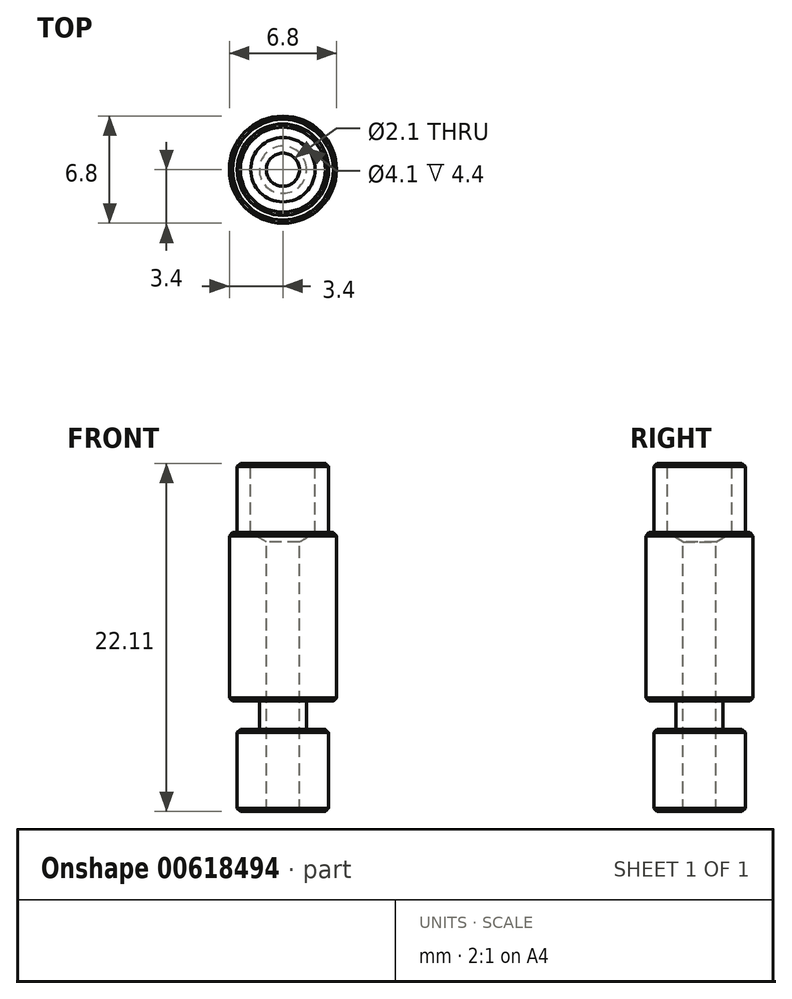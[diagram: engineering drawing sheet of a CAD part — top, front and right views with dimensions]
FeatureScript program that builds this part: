
annotation { "Feature Type Name" : "Feature", "Feature Type Description" : "" }
export const myFeature = defineFeature(function(context is Context, id is Id, definition is map)
    precondition{}
    {
        {
            var Q0;
            Q0=qCreatedBy(makeId("Top.planeOp"),FACE);
            var sketch = newSketch(context, id + "F0", { "sketchPlane" : qUnion([Q0])});
            skCircle(sketch, "E0", {"center": v(0, 0) * mm, "radius": 1.5 * mm});
            skCircle(sketch, "E1", {"center": v(0, 0) * mm, "radius": 2.9 * mm});
            skCircle(sketch, "E2", {"center": v(0, 0) * mm, "radius": 3.4 * mm});
            skSolve(sketch);
        }
        {
            var Q0;
            Q0=makeQuery(id+"F0.imprint","IMPRINT",FACE,{"disambiguationData":[TD([[makeQuery(id+"F0.imprint","IMPRINT",EDGE,{"derivedFrom":sQuery(id+"F0.wireOp",EDGE,"E0")}),-1.0]])]});
            var Q1;
            Q1=makeQuery(id+"F0.imprint","IMPRINT",FACE,{"disambiguationData":[TD([[makeQuery(id+"F0.imprint","IMPRINT",EDGE,{"derivedFrom":sQuery(id+"F0.wireOp",EDGE,"E0")}),1.0]])]});
            extrude(context, id + "F1", {"entities" : qUnion([Q0, Q1]), "depth" : 22.1 * mm, "offsetDistance" : 25 * mm});
        }
        {
            var Q0;
            Q0=makeQuery(id+"F0.imprint","IMPRINT",FACE,{"disambiguationData":[TD([[makeQuery(id+"F0.imprint","IMPRINT",EDGE,{"derivedFrom":sQuery(id+"F0.wireOp",EDGE,"E1")}),-1.0]])]});
            extrude(context, id + "F2", {"entities" : qUnion([Q0]), "operationType" : NewBodyOperationType.ADD, "depth" : 17.7 * mm, "offsetDistance" : 25 * mm, "hasSecondDirection" : true, "secondDirectionOppositeDirection" : false, "secondDirectionDepth" : 7 * mm});
        }
        {
            var Q0;
            Q0=makeQuery(id+"F0.imprint","IMPRINT",FACE,{"disambiguationData":[TD([[makeQuery(id+"F0.imprint","IMPRINT",EDGE,{"derivedFrom":sQuery(id+"F0.wireOp",EDGE,"E1")}),-1.0]])]});
            var Q1;
            Q1=makeQuery(id+"F0.imprint","IMPRINT",FACE,{"disambiguationData":[TD([[makeQuery(id+"F0.imprint","IMPRINT",EDGE,{"derivedFrom":sQuery(id+"F0.wireOp",EDGE,"E0")}),-1.0]])]});
            var Q2;
            Q2=makeQuery(id+"F2.opExtrude","CAP_FACE",FACE,{"disambiguationData":[OSD([sQuery(id+"F0.wireOp",EDGE,"E1"),sQuery(id+"F0.wireOp",EDGE,"E2")])],"isStart":true});
            extrude(context, id + "F3", {"entities" : qUnion([Q0, Q1]), "operationType" : NewBodyOperationType.REMOVE, "endBound" : BoundingType.UP_TO_SURFACE, "depth" : 12 * mm, "endBoundEntityFace" : qUnion([Q2]), "offsetDistance" : 25 * mm, "hasSecondDirection" : true, "secondDirectionOppositeDirection" : false, "secondDirectionDepth" : 5.2 * mm});
        }
        {
            var Q0;
            Q0=makeQuery(id+"F1.opExtrude","CAP_FACE",FACE,{"disambiguationData":[OSD([sQuery(id+"F0.wireOp",EDGE,"E1")])],"isStart":false});
            var sketch = newSketch(context, id + "F4", { "sketchPlane" : qUnion([Q0])});
            skPoint(sketch, "E3", {"position": v(0, 0) * mm});
            skSolve(sketch);
        }
        {
            var Q0;
            Q0=sQuery(id+"F4.wireOp",VERTEX,"E3");
            var Q1;
            Q1=makeQuery(id+"F1.opExtrude","SWEPT_BODY",BODY,{"disambiguationData":[OSD([sQuery(id+"F0.wireOp",EDGE,"E1")])]});
            hole(context, id + "F5", {"style" : HoleStyle.SIMPLE, "endStyle" : HoleEndStyle.THROUGH, "holeDiameter" : 2.1 * mm, "majorDiameter" : 5 * mm, "isTappedThrough" : true, "tappedDepth" : 12 * mm, "tapClearance" : 3, "locations" : qUnion([Q0]), "scope" : qUnion([Q1])});
        }
        {
            var Q0;
            Q0=sQuery(id+"F4.wireOp",VERTEX,"E3");
            var Q1;
            Q1=makeQuery(id+"F1.opExtrude","SWEPT_BODY",BODY,{"disambiguationData":[OSD([sQuery(id+"F0.wireOp",EDGE,"E1")])]});
            hole(context, id + "F6", {"style" : HoleStyle.SIMPLE, "endStyle" : HoleEndStyle.BLIND, "holeDiameter" : 4.1 * mm, "majorDiameter" : 5 * mm, "holeDepth" : 4.4 * mm, "isTappedThrough" : true, "tappedDepth" : 12 * mm, "tapClearance" : 3, "locations" : qUnion([Q0]), "scope" : qUnion([Q1])});
        }
        {
            var Q0;
            Q0=makeQuery(id+"F1.opExtrude","CAP_EDGE",EDGE,{"disambiguationData":[OSD([sQuery(id+"F0.wireOp",EDGE,"E1")])],"isStart":false});
            var Q1;
            {var subQ0=sQuery(id+"F0.wireOp",EDGE,"E2");var subQ1=sQuery(id+"F0.wireOp",EDGE,"E1");Q1=makeQuery(id+"F3.boolean.opBoolean","INTERSECT",EDGE,{"derivedFrom":[makeQuery(id+"F2.boolean.opBoolean","SPLIT",FACE,{"disambiguationData":[TD([makeQuery(id+"F1.opExtrude","CAP_FACE",FACE,{"disambiguationData":[OSD([subQ1])],"isStart":true})])],"derivedFrom":makeQuery(id+"F1.opExtrude","SWEPT_FACE",FACE,{"disambiguationData":[OSD([subQ1])]})}),makeQuery(id+"F3.opExtrude","CAP_FACE",FACE,{"disambiguationData":[OSD([sQuery(id+"F0.wireOp",EDGE,"E0"),subQ0])],"isStart":true})]});}
            var Q2;
            Q2=makeQuery(id+"F1.opExtrude","CAP_EDGE",EDGE,{"disambiguationData":[OSD([sQuery(id+"F0.wireOp",EDGE,"E1")])],"isStart":true});
            var Q3;
            Q3=makeQuery(id+"F2.opExtrude","CAP_EDGE",EDGE,{"disambiguationData":[OSD([sQuery(id+"F0.wireOp",EDGE,"E2")])],"isStart":true});
            var Q4;
            Q4=makeQuery(id+"F2.opExtrude","CAP_EDGE",EDGE,{"disambiguationData":[OSD([sQuery(id+"F0.wireOp",EDGE,"E2")])],"isStart":false});
            var Q5;
            Q5=makeQuery(id+"F6.hole-0.boolean.opBoolean","COPY",EDGE,{"derivedFrom":makeQuery(id+"F6.hole-0.opRevolve","SWEPT_EDGE",EDGE,{"disambiguationData":[OSD([sQuery(id+"F6.hole-0.sketch.wireOp",EDGE,"core_line_2"),sQuery(id+"F6.hole-0.sketch.wireOp",EDGE,"core_line_3")])]})});
            chamfer(context, id + "F7", {"entities" : qUnion([Q0, Q1, Q2, Q3, Q4, Q5]), "width" : 0.2 * mm, "tangentPropagation" : true});
        }
    });
